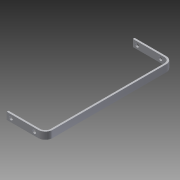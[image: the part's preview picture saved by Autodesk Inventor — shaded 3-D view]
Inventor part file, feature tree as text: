
AUTODESK INVENTOR PART (.ipt)
format: ipt  version: 2013 (Build 170138000, 138)  size: 122,880 bytes
history: native  units: in
note: dims shown in document units (in); Inventor stores cm internally (conversion verified against a paired STEP export)
features: sheet_metal_op x7, sketch x4, other x3, extrude x1
ambient origin geometry x8: Origin, YZ Plane, XZ Plane, XY Plane, X Axis, Y Axis, Z Axis, Center Point
bodies: Solid1 (feature_tree)
feature tree (15):
  sheet_metal_op  "Face1"
  sheet_metal_op  "Flange2"
  sheet_metal_op  "Flange3"
  extrude  "Extrusion1"  Depth=0.5in
  sketch  "Sketch1"  dims[d1=2.244in d2=0.5in]
  other  "Plate1"
  sketch  "Sketch3"  dims[d3=0.295in]
  other  "Plate3"
  sheet_metal_op  "Bend2"
  sheet_metal_op  "Corner2"
  sketch  "Sketch4"  dims[d4=0.25in]
  other  "Plate4"
  sheet_metal_op  "Bend3"
  sheet_metal_op  "Corner3"
  sketch  "Sketch5"  dims[d5=0.295in d6=0.26in d7=0.26in d8=0.125in d19=0.25in d20=0.125in d21=0.0625in d22=0.25in d23=0.125in d24=8.572in d25=90.0deg d26=0.375in d27=0.5in d28=0.125in d29=0.125in d30=0.125in d31=0.0625in d32=0.25in d33=0.125in d34=2.744in d35=90.0deg d36=0.375in d37=0.5in d38=0.125in d39=0.125in d40=90.0in d41=0.0in]
